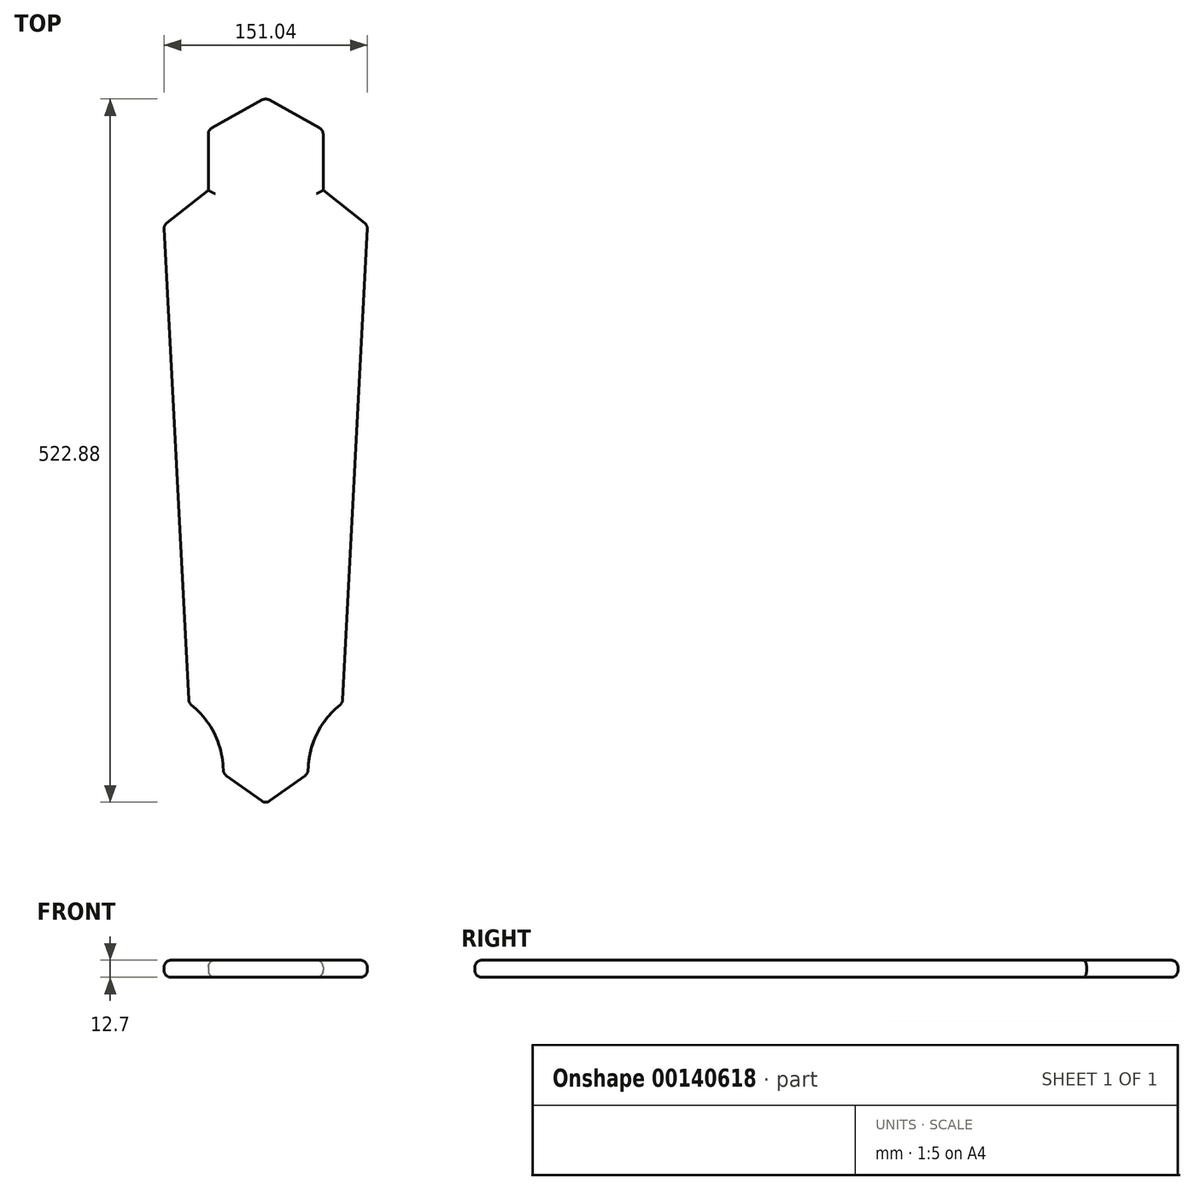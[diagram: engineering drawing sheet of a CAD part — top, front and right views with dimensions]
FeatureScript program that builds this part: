
annotation { "Feature Type Name" : "Feature", "Feature Type Description" : "" }
export const myFeature = defineFeature(function(context is Context, id is Id, definition is map)
    precondition{}
    {
        {
            var Q0;
            Q0=qCreatedBy(makeId("Top.planeOp"),FACE);
            var sketch = newSketch(context, id + "F0", { "sketchPlane" : qUnion([Q0])});
            skPoint(sketch, "E0.middle", {"position": v(0, 0) * mm});
            skPoint(sketch, "E1.endSnap0", {"position": v(0, 165.1) * mm});
            skLineSegment(sketch, "E2", {"start": v(-76.98, 160.7) * mm, "end": v(-44.03, 186.6) * mm});
            skLineSegment(sketch, "E3", {"start": v(-44.03, 186.6) * mm, "end": v(-44.03, 231.47) * mm});
            skLineSegment(sketch, "E4", {"start": v(-44.03, 231.47) * mm, "end": v(-1.33, 255.27) * mm});
            skLineSegment(sketch, "E5", {"start": v(-76.98, 160.7) * mm, "end": v(-58.48, -194.42) * mm});
            skFitSpline(sketch, "E6", {"points": [v(-58.48, -194.42) * mm, v(-32.8, -246.95) * mm], "startDerivative": vector(35.78, -28.37) * mm, "endDerivative": vector(0.61, -81.84) * mm});
            skLineSegment(sketch, "E7", {"start": v(-32.8, -246.95) * mm, "end": v(-1.33, -269.52) * mm});
            skLineSegment(sketch, "E8.MirrorCS", {"start": v(41.37, 231.47) * mm, "end": v(-1.33, 255.27) * mm});
            skLineSegment(sketch, "E9.MirrorCS", {"start": v(41.37, 186.6) * mm, "end": v(41.37, 231.47) * mm});
            skLineSegment(sketch, "E10.MirrorCS", {"start": v(74.32, 160.7) * mm, "end": v(41.37, 186.6) * mm});
            skLineSegment(sketch, "E11.MirrorCS", {"start": v(74.32, 160.7) * mm, "end": v(55.82, -194.42) * mm});
            skFitSpline(sketch, "E12.MirrorCS", {"points": [v(55.82, -194.42) * mm, v(30.12, -246.95) * mm], "startDerivative": vector(-35.78, -28.37) * mm, "endDerivative": vector(-0.61, -81.84) * mm});
            skLineSegment(sketch, "E13.MirrorCS", {"start": v(30.12, -246.95) * mm, "end": v(-1.33, -269.52) * mm});
            skSolve(sketch);
        }
        {
            var Q0;
            Q0=makeQuery(id+"F0.imprint","IMPRINT",FACE,{"disambiguationData":[TD([[makeQuery(id+"F0.imprint","IMPRINT",EDGE,{"derivedFrom":sQuery(id+"F0.wireOp",EDGE,"E2")}),-1.0]])]});
            extrude(context, id + "F1", {"entities" : qUnion([Q0]), "depth" : 12.7 * mm});
        }
        {
            var Q0;
            Q0=makeQuery(id+"F1.opExtrude","CAP_EDGE",EDGE,{"disambiguationData":[OSD([sQuery(id+"F0.wireOp",EDGE,"E5")])],"isStart":false});
            var Q1;
            Q1=makeQuery(id+"F1.opExtrude","CAP_EDGE",EDGE,{"disambiguationData":[OSD([sQuery(id+"F0.wireOp",EDGE,"E6")])],"isStart":false});
            var Q2;
            Q2=makeQuery(id+"F1.opExtrude","CAP_EDGE",EDGE,{"disambiguationData":[OSD([sQuery(id+"F0.wireOp",EDGE,"E7")])],"isStart":false});
            var Q3;
            Q3=makeQuery(id+"F1.opExtrude","CAP_EDGE",EDGE,{"disambiguationData":[OSD([sQuery(id+"F0.wireOp",EDGE,"E13.MirrorCS")])],"isStart":false});
            var Q4;
            Q4=makeQuery(id+"F1.opExtrude","CAP_EDGE",EDGE,{"disambiguationData":[OSD([sQuery(id+"F0.wireOp",EDGE,"E12.MirrorCS")])],"isStart":false});
            var Q5;
            Q5=makeQuery(id+"F1.opExtrude","CAP_EDGE",EDGE,{"disambiguationData":[OSD([sQuery(id+"F0.wireOp",EDGE,"E11.MirrorCS")])],"isStart":false});
            var Q6;
            Q6=makeQuery(id+"F1.opExtrude","CAP_EDGE",EDGE,{"disambiguationData":[OSD([sQuery(id+"F0.wireOp",EDGE,"E10.MirrorCS")])],"isStart":false});
            var Q7;
            Q7=makeQuery(id+"F1.opExtrude","CAP_EDGE",EDGE,{"disambiguationData":[OSD([sQuery(id+"F0.wireOp",EDGE,"E2")])],"isStart":false});
            var Q8;
            Q8=makeQuery(id+"F1.opExtrude","CAP_EDGE",EDGE,{"disambiguationData":[OSD([sQuery(id+"F0.wireOp",EDGE,"E3")])],"isStart":false});
            var Q9;
            Q9=makeQuery(id+"F1.opExtrude","CAP_EDGE",EDGE,{"disambiguationData":[OSD([sQuery(id+"F0.wireOp",EDGE,"E9.MirrorCS")])],"isStart":false});
            var Q10;
            Q10=makeQuery(id+"F1.opExtrude","CAP_EDGE",EDGE,{"disambiguationData":[OSD([sQuery(id+"F0.wireOp",EDGE,"E8.MirrorCS")])],"isStart":false});
            var Q11;
            Q11=makeQuery(id+"F1.opExtrude","CAP_EDGE",EDGE,{"disambiguationData":[OSD([sQuery(id+"F0.wireOp",EDGE,"E4")])],"isStart":false});
            fillet(context, id + "F2", {"entities" : qUnion([Q0, Q1, Q2, Q3, Q4, Q5, Q6, Q7, Q8, Q9, Q10, Q11]), "radius" : 5.08 * mm, "tangentPropagation" : true, "allowEdgeOverflow" : false});
        }
        {
            var Q0;
            Q0=makeQuery(id+"F1.opExtrude","CAP_EDGE",EDGE,{"disambiguationData":[OSD([sQuery(id+"F0.wireOp",EDGE,"E11.MirrorCS")])],"isStart":true});
            var Q1;
            Q1=makeQuery(id+"F1.opExtrude","CAP_EDGE",EDGE,{"disambiguationData":[OSD([sQuery(id+"F0.wireOp",EDGE,"E5")])],"isStart":true});
            var Q2;
            Q2=makeQuery(id+"F1.opExtrude","CAP_EDGE",EDGE,{"disambiguationData":[OSD([sQuery(id+"F0.wireOp",EDGE,"E2")])],"isStart":true});
            var Q3;
            Q3=makeQuery(id+"F1.opExtrude","CAP_EDGE",EDGE,{"disambiguationData":[OSD([sQuery(id+"F0.wireOp",EDGE,"E3")])],"isStart":true});
            var Q4;
            Q4=makeQuery(id+"F1.opExtrude","CAP_EDGE",EDGE,{"disambiguationData":[OSD([sQuery(id+"F0.wireOp",EDGE,"E4")])],"isStart":true});
            var Q5;
            Q5=makeQuery(id+"F1.opExtrude","CAP_EDGE",EDGE,{"disambiguationData":[OSD([sQuery(id+"F0.wireOp",EDGE,"E8.MirrorCS")])],"isStart":true});
            var Q6;
            Q6=makeQuery(id+"F1.opExtrude","CAP_EDGE",EDGE,{"disambiguationData":[OSD([sQuery(id+"F0.wireOp",EDGE,"E9.MirrorCS")])],"isStart":true});
            var Q7;
            Q7=makeQuery(id+"F1.opExtrude","CAP_EDGE",EDGE,{"disambiguationData":[OSD([sQuery(id+"F0.wireOp",EDGE,"E10.MirrorCS")])],"isStart":true});
            var Q8;
            Q8=makeQuery(id+"F1.opExtrude","CAP_EDGE",EDGE,{"disambiguationData":[OSD([sQuery(id+"F0.wireOp",EDGE,"E12.MirrorCS")])],"isStart":true});
            var Q9;
            Q9=makeQuery(id+"F1.opExtrude","CAP_EDGE",EDGE,{"disambiguationData":[OSD([sQuery(id+"F0.wireOp",EDGE,"E6")])],"isStart":true});
            var Q10;
            Q10=makeQuery(id+"F1.opExtrude","CAP_EDGE",EDGE,{"disambiguationData":[OSD([sQuery(id+"F0.wireOp",EDGE,"E7")])],"isStart":true});
            var Q11;
            Q11=makeQuery(id+"F1.opExtrude","CAP_EDGE",EDGE,{"disambiguationData":[OSD([sQuery(id+"F0.wireOp",EDGE,"E13.MirrorCS")])],"isStart":true});
            fillet(context, id + "F3", {"entities" : qUnion([Q0, Q1, Q2, Q3, Q4, Q5, Q6, Q7, Q8, Q9, Q10, Q11]), "radius" : 5.08 * mm, "tangentPropagation" : true, "allowEdgeOverflow" : false});
        }
        {
            var Q0;
            Q0=makeQuery(id+"F1.opExtrude","SWEPT_EDGE",EDGE,{"disambiguationData":[OSD([sQuery(id+"F0.wireOp",EDGE,"E4"),sQuery(id+"F0.wireOp",EDGE,"E8.MirrorCS")])]});
            var Q1;
            Q1=makeQuery(id+"F1.opExtrude","SWEPT_EDGE",EDGE,{"disambiguationData":[OSD([sQuery(id+"F0.wireOp",EDGE,"E8.MirrorCS"),sQuery(id+"F0.wireOp",EDGE,"E9.MirrorCS")])]});
            var Q2;
            Q2=makeQuery(id+"F1.opExtrude","SWEPT_EDGE",EDGE,{"disambiguationData":[OSD([sQuery(id+"F0.wireOp",EDGE,"E10.MirrorCS"),sQuery(id+"F0.wireOp",EDGE,"E11.MirrorCS")])]});
            var Q3;
            Q3=makeQuery(id+"F1.opExtrude","SWEPT_EDGE",EDGE,{"disambiguationData":[OSD([sQuery(id+"F0.wireOp",EDGE,"E3"),sQuery(id+"F0.wireOp",EDGE,"E4")])]});
            var Q4;
            Q4=makeQuery(id+"F1.opExtrude","SWEPT_EDGE",EDGE,{"disambiguationData":[OSD([sQuery(id+"F0.wireOp",EDGE,"E2"),sQuery(id+"F0.wireOp",EDGE,"E5")])]});
            var Q5;
            Q5=makeQuery(id+"F1.opExtrude","SWEPT_EDGE",EDGE,{"disambiguationData":[OSD([sQuery(id+"F0.wireOp",EDGE,"E5"),sQuery(id+"F0.wireOp",EDGE,"E6")])]});
            var Q6;
            Q6=makeQuery(id+"F1.opExtrude","SWEPT_EDGE",EDGE,{"disambiguationData":[OSD([sQuery(id+"F0.wireOp",EDGE,"E6"),sQuery(id+"F0.wireOp",EDGE,"E7")])]});
            var Q7;
            Q7=makeQuery(id+"F1.opExtrude","SWEPT_EDGE",EDGE,{"disambiguationData":[OSD([sQuery(id+"F0.wireOp",EDGE,"E7"),sQuery(id+"F0.wireOp",EDGE,"E13.MirrorCS")])]});
            var Q8;
            Q8=makeQuery(id+"F1.opExtrude","SWEPT_EDGE",EDGE,{"disambiguationData":[OSD([sQuery(id+"F0.wireOp",EDGE,"E12.MirrorCS"),sQuery(id+"F0.wireOp",EDGE,"E13.MirrorCS")])]});
            var Q9;
            Q9=makeQuery(id+"F1.opExtrude","SWEPT_EDGE",EDGE,{"disambiguationData":[OSD([sQuery(id+"F0.wireOp",EDGE,"E11.MirrorCS"),sQuery(id+"F0.wireOp",EDGE,"E12.MirrorCS")])]});
            fillet(context, id + "F4", {"entities" : qUnion([Q0, Q1, Q2, Q3, Q4, Q5, Q6, Q7, Q8, Q9]), "radius" : 5.08 * mm, "tangentPropagation" : true, "allowEdgeOverflow" : false});
        }
    });
